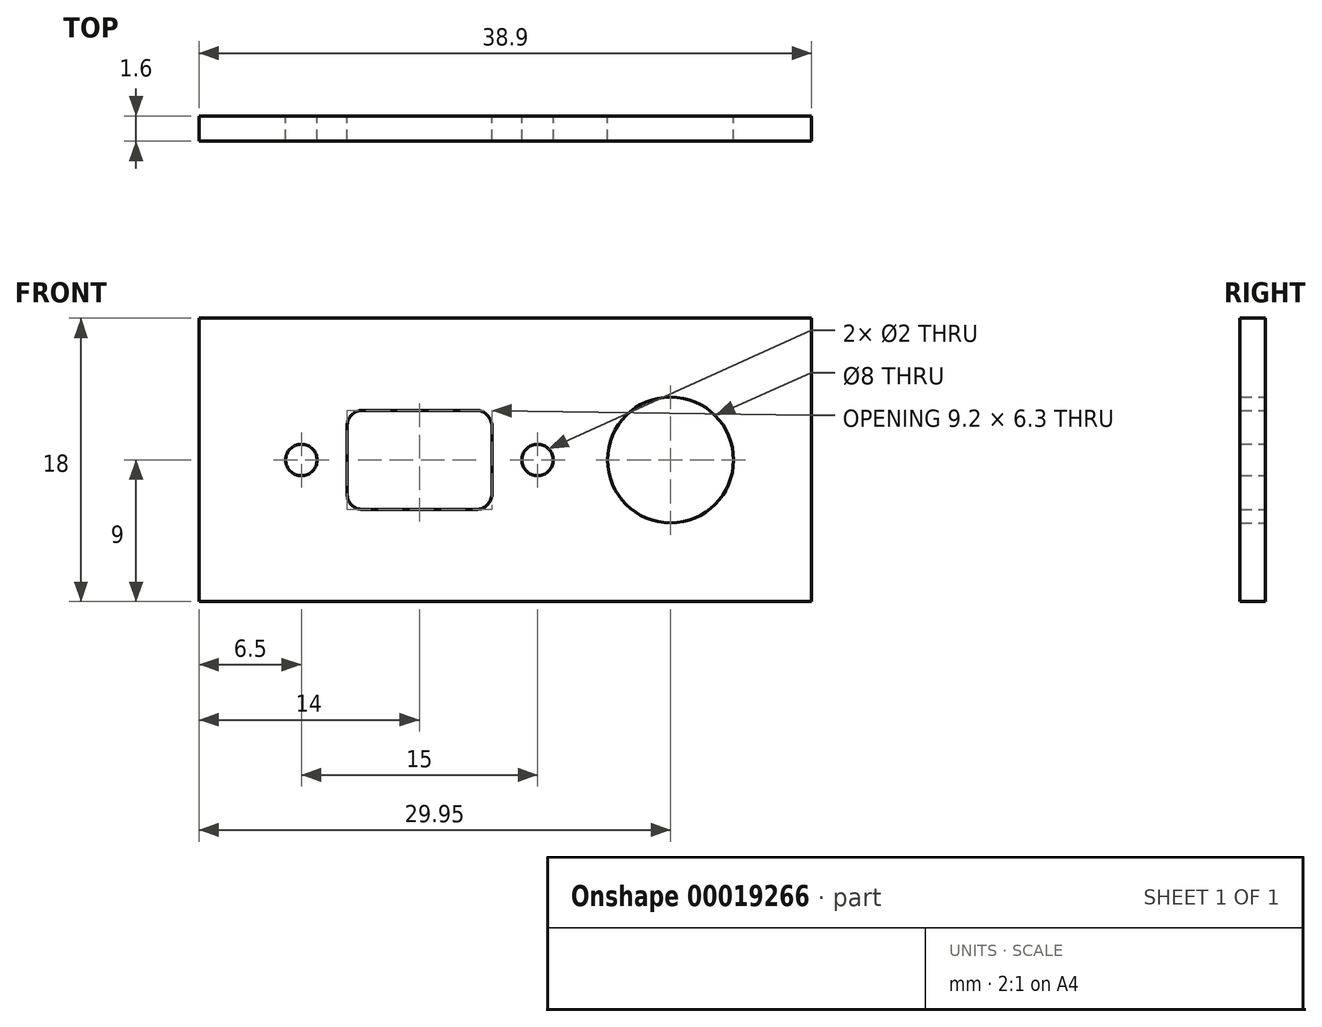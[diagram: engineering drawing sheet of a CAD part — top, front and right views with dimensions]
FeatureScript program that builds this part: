
annotation { "Feature Type Name" : "Feature", "Feature Type Description" : "" }
export const myFeature = defineFeature(function(context is Context, id is Id, definition is map)
    precondition{}
    {
        {
            var Q0;
            Q0=qCreatedBy(makeId("Front.planeOp"),FACE);
            var sketch = newSketch(context, id + "F0", { "sketchPlane" : qUnion([Q0])});
            skLineSegment(sketch, "E0.rect.bottom", {"start": v(3.6, 3.15) * mm, "end": v(-3.6, 3.15) * mm});
            skLineSegment(sketch, "E0.rect.top", {"start": v(3.6, -3.15) * mm, "end": v(-3.6, -3.15) * mm});
            skLineSegment(sketch, "E0.rect.left", {"start": v(4.6, 2.15) * mm, "end": v(4.6, -2.15) * mm});
            skLineSegment(sketch, "E0.rect.right", {"start": v(-4.6, 2.15) * mm, "end": v(-4.6, -2.15) * mm});
            skPoint(sketch, "E0.rect.middle", {"position": v(0, 0) * mm});
            skLineSegment(sketch, "E1.rect.bottom", {"start": v(10, 5) * mm, "end": v(-10, 5) * mm, "construction": true});
            skLineSegment(sketch, "E1.rect.top", {"start": v(10, -5) * mm, "end": v(-10, -5) * mm, "construction": true});
            skLineSegment(sketch, "E1.rect.left", {"start": v(10, 5) * mm, "end": v(10, -5) * mm, "construction": true});
            skLineSegment(sketch, "E1.rect.right", {"start": v(-10, 5) * mm, "end": v(-10, -5) * mm, "construction": true});
            skCircle(sketch, "E2", {"center": v(-7.5, 0) * mm, "radius": 1 * mm});
            skCircle(sketch, "E3", {"center": v(7.5, 0) * mm, "radius": 1 * mm});
            skCircle(sketch, "E4", {"center": v(15.95, 0) * mm, "radius": 4 * mm});
            skCircle(sketch, "E5", {"center": v(15.95, 0) * mm, "radius": 4.95 * mm, "construction": true});
            skPoint(sketch, "E6.visualSharp", {"position": v(-4.6, 3.15) * mm});
            skArc(sketch, "E6.filletArc", {"start": v(-3.6, 3.15) * mm, "mid": v(-4.3, 2.86) * mm, "end": v(-4.6, 2.15) * mm});
            skPoint(sketch, "E7.visualSharp", {"position": v(4.6, 3.15) * mm});
            skArc(sketch, "E7.filletArc", {"start": v(4.6, 2.15) * mm, "mid": v(4.3, 2.86) * mm, "end": v(3.6, 3.15) * mm});
            skPoint(sketch, "E8.visualSharp", {"position": v(4.6, -3.15) * mm});
            skArc(sketch, "E8.filletArc", {"start": v(3.6, -3.15) * mm, "mid": v(4.3, -2.86) * mm, "end": v(4.6, -2.15) * mm});
            skPoint(sketch, "E9.visualSharp", {"position": v(-4.6, -3.15) * mm});
            skArc(sketch, "E9.filletArc", {"start": v(-4.6, -2.15) * mm, "mid": v(-4.3, -2.86) * mm, "end": v(-3.6, -3.15) * mm});
            skLineSegment(sketch, "E10.bottom", {"start": v(-14, -9) * mm, "end": v(24.9, -9) * mm});
            skLineSegment(sketch, "E10.top", {"start": v(-14, 9) * mm, "end": v(24.9, 9) * mm});
            skLineSegment(sketch, "E10.left", {"start": v(-14, -9) * mm, "end": v(-14, 9) * mm});
            skLineSegment(sketch, "E10.right", {"start": v(24.9, -9) * mm, "end": v(24.9, 9) * mm});
            skSolve(sketch);
        }
        {
            var Q0;
            Q0 = qSketchRegion(id + "F0", true);
            extrude(context, id + "F1", {"entities" : qUnion([Q0]), "depth" : 1.6 * mm});
        }
    });
